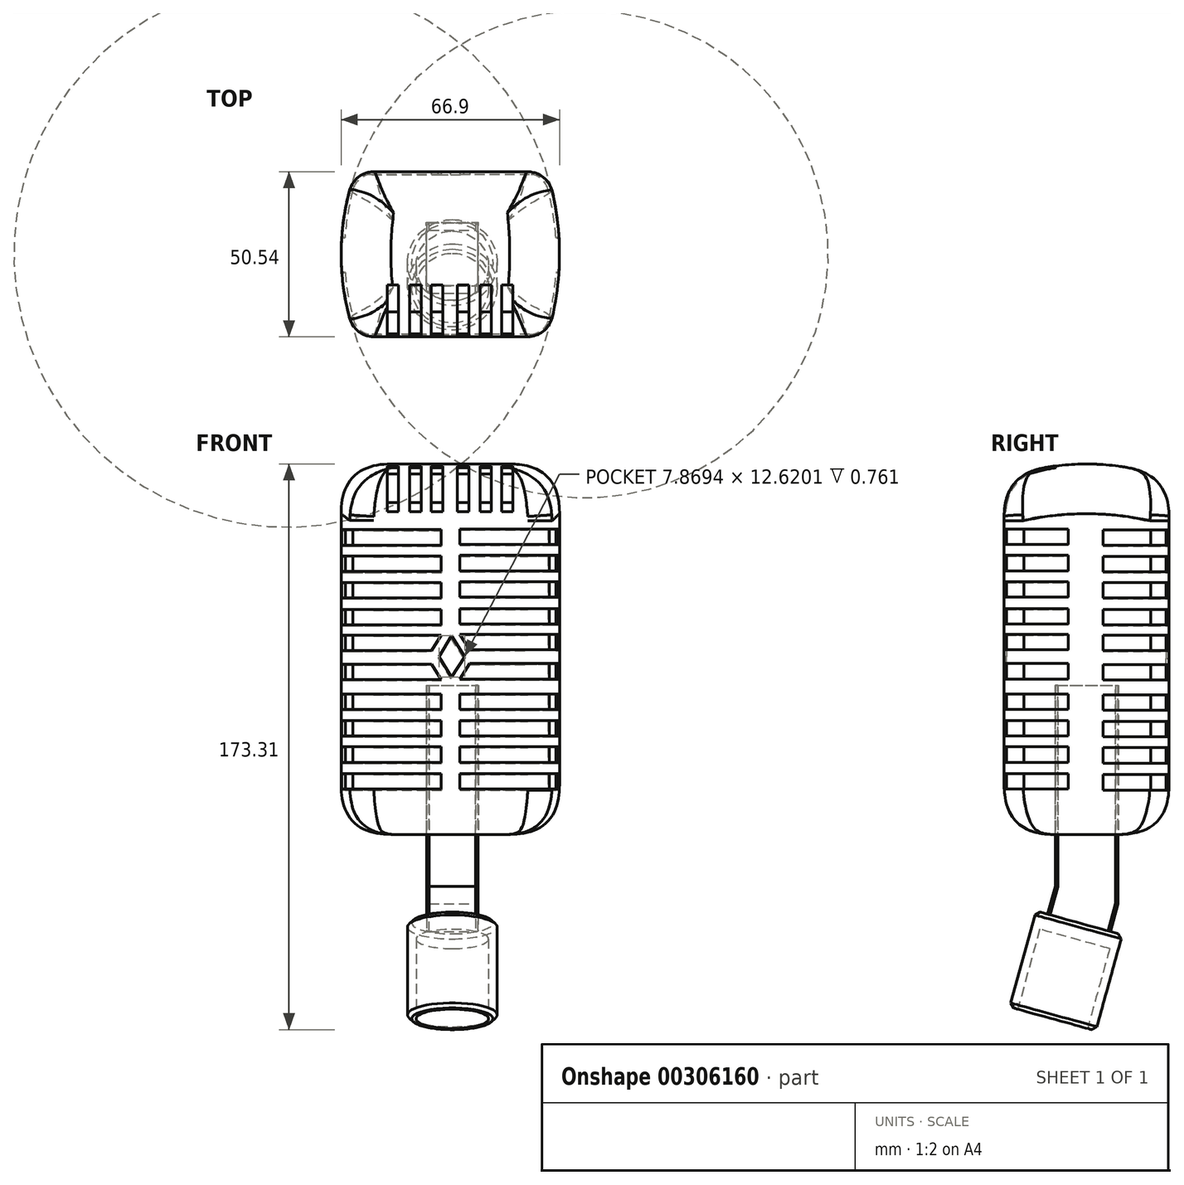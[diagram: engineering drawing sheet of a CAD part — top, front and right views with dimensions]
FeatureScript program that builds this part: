
annotation { "Feature Type Name" : "Feature", "Feature Type Description" : "" }
export const myFeature = defineFeature(function(context is Context, id is Id, definition is map)
    precondition{}
    {
        {
            var Q0;
            Q0=qCreatedBy(makeId("Top.planeOp"),FACE);
            var sketch = newSketch(context, id + "F0", { "sketchPlane" : qUnion([Q0])});
            skLineSegment(sketch, "E0.bottom", {"start": v(-44.56, 25.27) * mm, "end": v(14.03, 25.27) * mm});
            skLineSegment(sketch, "E0.top", {"start": v(-44.56, -25.27) * mm, "end": v(14.03, -25.27) * mm});
            skLineSegment(sketch, "E0.left", {"start": v(-44.56, 25.27) * mm, "end": v(-44.56, -25.27) * mm});
            skLineSegment(sketch, "E0.right", {"start": v(14.03, 25.27) * mm, "end": v(14.03, -25.27) * mm});
            skArc(sketch, "E1", {"start": v(-44.56, 25.27) * mm, "mid": v(-48.96, 0) * mm, "end": v(-44.56, -25.27) * mm});
            skArc(sketch, "E2", {"start": v(14.03, -25.27) * mm, "mid": v(17.94, 0) * mm, "end": v(14.03, 25.27) * mm});
            skSolve(sketch);
        }
        {
            var Q0;
            Q0 = qSketchRegion(id + "F0", true);
            extrude(context, id + "F1", {"entities" : qUnion([Q0]), "depth" : 61.72 * mm, "hasSecondDirection" : true, "secondDirectionOppositeDirection" : true, "secondDirectionDepth" : 52.58 * mm});
        }
        {
            var Q0;
            Q0=qCreatedBy(makeId("Right.planeOp"),FACE);
            cPlane(context, id + "F2", {"entities" : qUnion([Q0]), "cplaneType" : CPlaneType.OFFSET, "offset" : 66.55 * mm, "width" : 152.4 * mm, "height" : 152.4 * mm});
        }
        {
            var Q0;
            Q0=qCreatedBy(id+"F2.planeOp",FACE);
            var sketch = newSketch(context, id + "F3", { "sketchPlane" : qUnion([Q0])});
            skArc(sketch, "E3", {"start": v(-32.43, -60.12) * mm, "mid": v(-0.42, -66.6) * mm, "end": v(31.59, -60.12) * mm});
            skArc(sketch, "E4", {"start": v(31.64, 53.76) * mm, "mid": v(-0.1, 60.92) * mm, "end": v(-31.84, 53.76) * mm});
            skLineSegment(sketch, "E5", {"start": v(-31.84, 53.76) * mm, "end": v(-36.54, 47.04) * mm});
            skLineSegment(sketch, "E6", {"start": v(-36.54, 47.04) * mm, "end": v(-36.54, -49.58) * mm});
            skLineSegment(sketch, "E7", {"start": v(-36.54, -49.58) * mm, "end": v(-32.43, -60.12) * mm});
            skLineSegment(sketch, "E8", {"start": v(31.59, -60.12) * mm, "end": v(40.36, -46.04) * mm});
            skLineSegment(sketch, "E9", {"start": v(40.36, -46.04) * mm, "end": v(40.36, 46.53) * mm});
            skLineSegment(sketch, "E10", {"start": v(40.36, 46.53) * mm, "end": v(31.64, 53.76) * mm});
            skLineSegment(sketch, "E11.bottom", {"start": v(-51.4, 74.25) * mm, "end": v(55.8, 74.25) * mm});
            skLineSegment(sketch, "E11.top", {"start": v(-51.4, -75.1) * mm, "end": v(55.8, -75.1) * mm});
            skLineSegment(sketch, "E11.left", {"start": v(-51.4, 74.25) * mm, "end": v(-51.4, -75.1) * mm});
            skLineSegment(sketch, "E11.right", {"start": v(55.8, 74.25) * mm, "end": v(55.8, -75.1) * mm});
            skSolve(sketch);
        }
        {
            var Q0;
            Q0=makeQuery(id+"F3.imprint","IMPRINT",FACE,{"disambiguationData":[TD([[makeQuery(id+"F3.imprint","IMPRINT",EDGE,{"derivedFrom":sQuery(id+"F3.wireOp",EDGE,"E3")}),-1.0]])]});
            extrude(context, id + "F4", {"entities" : qUnion([Q0]), "operationType" : NewBodyOperationType.REMOVE, "oppositeDirection" : true, "depth" : 198.37 * mm});
        }
        {
            var Q0;
            Q0=makeQuery(id+"F1.opExtrude","SWEPT_EDGE",EDGE,{"disambiguationData":[OSD([sQuery(id+"F0.wireOp",EDGE,"E0.top"),sQuery(id+"F0.wireOp",EDGE,"E0.right"),sQuery(id+"F0.wireOp",EDGE,"E2")])]});
            var Q1;
            Q1=makeQuery(id+"F1.opExtrude","SWEPT_EDGE",EDGE,{"disambiguationData":[OSD([sQuery(id+"F0.wireOp",EDGE,"E0.bottom"),sQuery(id+"F0.wireOp",EDGE,"E0.right"),sQuery(id+"F0.wireOp",EDGE,"E2")])]});
            var Q2;
            Q2=makeQuery(id+"F1.opExtrude","SWEPT_EDGE",EDGE,{"disambiguationData":[OSD([sQuery(id+"F0.wireOp",EDGE,"E0.top"),sQuery(id+"F0.wireOp",EDGE,"E0.left"),sQuery(id+"F0.wireOp",EDGE,"E1")])]});
            var Q3;
            Q3=makeQuery(id+"F1.opExtrude","SWEPT_EDGE",EDGE,{"disambiguationData":[OSD([sQuery(id+"F0.wireOp",EDGE,"E0.bottom"),sQuery(id+"F0.wireOp",EDGE,"E0.left"),sQuery(id+"F0.wireOp",EDGE,"E1")])]});
            fillet(context, id + "F5", {"entities" : qUnion([Q0, Q1, Q2, Q3]), "radius" : 7.62 * mm, "tangentPropagation" : true, "allowEdgeOverflow" : false});
        }
        {
            var Q0;
            Q0=makeQuery(id+"F4.boolean.opBoolean","COPY",FACE,{"derivedFrom":makeQuery(id+"F4.opExtrude","SWEPT_FACE",FACE,{"disambiguationData":[OSD([sQuery(id+"F3.wireOp",EDGE,"E4")])]})});
            var Q1;
            Q1=makeQuery(id+"F4.boolean.opBoolean","COPY",FACE,{"derivedFrom":makeQuery(id+"F4.opExtrude","SWEPT_FACE",FACE,{"disambiguationData":[OSD([sQuery(id+"F3.wireOp",EDGE,"E3")])]})});
            var Q2;
            Q2=makeQuery(id+"F1.opExtrude","CAP_FACE",FACE,{"disambiguationData":[OSD([sQuery(id+"F0.wireOp",EDGE,"E0.bottom"),sQuery(id+"F0.wireOp",EDGE,"E0.top"),sQuery(id+"F0.wireOp",EDGE,"E1"),sQuery(id+"F0.wireOp",EDGE,"E2")])],"isStart":true});
            fillet(context, id + "F6", {"entities" : qUnion([Q0, Q1, Q2]), "radius" : 15.24 * mm, "tangentPropagation" : true, "rho" : 0.5, "crossSection" : FilletCrossSection.CONIC, "allowEdgeOverflow" : false});
        }
        {
            var Q0;
            Q0=qCreatedBy(makeId("Front.planeOp"),FACE);
            cPlane(context, id + "F7", {"entities" : qUnion([Q0]), "cplaneType" : CPlaneType.OFFSET, "offset" : 55.63 * mm, "width" : 152.4 * mm, "height" : 152.4 * mm});
        }
        {
            var Q0;
            Q0=qCreatedBy(id+"F7.planeOp",FACE);
            var sketch = newSketch(context, id + "F8", { "sketchPlane" : qUnion([Q0])});
            skLineSegment(sketch, "E12.bottom", {"start": v(-13.3, 61.66) * mm, "end": v(-9.84, 61.66) * mm});
            skLineSegment(sketch, "E12.top", {"start": v(-13.3, 46.27) * mm, "end": v(-9.84, 46.27) * mm});
            skLineSegment(sketch, "E12.left", {"start": v(-13.3, 61.66) * mm, "end": v(-13.3, 46.27) * mm});
            skLineSegment(sketch, "E12.right", {"start": v(-9.84, 61.66) * mm, "end": v(-9.84, 46.27) * mm});
            skLineSegment(sketch, "E13.bottom", {"start": v(-6.4, 61.66) * mm, "end": v(-2.94, 61.66) * mm});
            skLineSegment(sketch, "E13.top", {"start": v(-6.4, 46.27) * mm, "end": v(-2.94, 46.27) * mm});
            skLineSegment(sketch, "E13.left", {"start": v(-6.4, 61.66) * mm, "end": v(-6.4, 46.27) * mm});
            skLineSegment(sketch, "E13.right", {"start": v(-2.94, 61.66) * mm, "end": v(-2.94, 46.27) * mm});
            skLineSegment(sketch, "E14.bottom", {"start": v(0.21, 61.66) * mm, "end": v(3.67, 61.66) * mm});
            skLineSegment(sketch, "E14.top", {"start": v(0.21, 46.27) * mm, "end": v(3.67, 46.27) * mm});
            skLineSegment(sketch, "E14.left", {"start": v(0.21, 61.66) * mm, "end": v(0.21, 46.27) * mm});
            skLineSegment(sketch, "E14.right", {"start": v(3.67, 61.66) * mm, "end": v(3.67, 46.27) * mm});
            skLineSegment(sketch, "E15.bottom", {"start": v(-34.83, 61.66) * mm, "end": v(-31.37, 61.66) * mm});
            skLineSegment(sketch, "E15.top", {"start": v(-34.83, 46.27) * mm, "end": v(-31.37, 46.27) * mm});
            skLineSegment(sketch, "E15.left", {"start": v(-34.83, 61.66) * mm, "end": v(-34.83, 46.27) * mm});
            skLineSegment(sketch, "E15.right", {"start": v(-31.37, 61.66) * mm, "end": v(-31.37, 46.27) * mm});
            skLineSegment(sketch, "E16.left", {"start": v(-27.93, 61.66) * mm, "end": v(-27.93, 46.27) * mm});
            skLineSegment(sketch, "E16.right", {"start": v(-24.47, 61.66) * mm, "end": v(-24.47, 46.27) * mm});
            skLineSegment(sketch, "E17.left", {"start": v(-21.32, 61.66) * mm, "end": v(-21.32, 46.27) * mm});
            skLineSegment(sketch, "E17.right", {"start": v(-17.86, 61.66) * mm, "end": v(-17.86, 46.27) * mm});
            skLineSegment(sketch, "E18", {"start": v(-27.93, 61.66) * mm, "end": v(-24.47, 61.66) * mm});
            skLineSegment(sketch, "E19", {"start": v(-21.32, 61.66) * mm, "end": v(-17.86, 61.66) * mm});
            skLineSegment(sketch, "E20", {"start": v(-27.93, 46.27) * mm, "end": v(-24.47, 46.27) * mm});
            skLineSegment(sketch, "E21", {"start": v(-21.32, 46.27) * mm, "end": v(-17.86, 46.27) * mm});
            skSolve(sketch);
        }
        {
            var Q0;
            Q0 = qSketchRegion(id + "F8", true);
            extrude(context, id + "F9", {"entities" : qUnion([Q0]), "operationType" : NewBodyOperationType.REMOVE, "oppositeDirection" : true, "depth" : 46.23 * mm});
        }
        {
            var Q0;
            Q0=qCreatedBy(id+"F7.planeOp",FACE);
            var sketch = newSketch(context, id + "F10", { "sketchPlane" : qUnion([Q0])});
            skLineSegment(sketch, "E22", {"start": v(-12.54, 41) * mm, "end": v(26.66, 41) * mm});
            skLineSegment(sketch, "E23", {"start": v(26.66, 41) * mm, "end": v(26.66, 36.27) * mm});
            skLineSegment(sketch, "E24", {"start": v(26.66, 36.27) * mm, "end": v(-12.54, 36.27) * mm});
            skLineSegment(sketch, "E25", {"start": v(-12.54, 36.27) * mm, "end": v(-12.54, 41) * mm});
            skLineSegment(sketch, "E26", {"start": v(-12.54, 32.91) * mm, "end": v(26.66, 32.91) * mm});
            skLineSegment(sketch, "E27", {"start": v(26.66, 32.91) * mm, "end": v(26.66, 28.18) * mm});
            skLineSegment(sketch, "E28", {"start": v(26.66, 28.18) * mm, "end": v(-12.54, 28.18) * mm});
            skLineSegment(sketch, "E29", {"start": v(-12.54, 28.18) * mm, "end": v(-12.54, 32.91) * mm});
            skLineSegment(sketch, "E30", {"start": v(-12.54, 24.84) * mm, "end": v(26.66, 24.84) * mm});
            skLineSegment(sketch, "E31", {"start": v(26.66, 24.84) * mm, "end": v(26.66, 20.11) * mm});
            skLineSegment(sketch, "E32", {"start": v(26.66, 20.11) * mm, "end": v(-12.54, 20.11) * mm});
            skLineSegment(sketch, "E33", {"start": v(-12.54, 20.11) * mm, "end": v(-12.54, 24.84) * mm});
            skLineSegment(sketch, "E34", {"start": v(-12.54, 16.61) * mm, "end": v(26.66, 16.61) * mm});
            skLineSegment(sketch, "E35", {"start": v(26.66, 16.61) * mm, "end": v(26.66, 11.88) * mm});
            skLineSegment(sketch, "E36", {"start": v(26.66, 11.88) * mm, "end": v(-12.54, 11.88) * mm});
            skLineSegment(sketch, "E37", {"start": v(-12.54, 11.88) * mm, "end": v(-12.54, 16.61) * mm});
            skLineSegment(sketch, "E38", {"start": v(-12.54, 8.72) * mm, "end": v(26.66, 8.72) * mm});
            skLineSegment(sketch, "E39", {"start": v(26.66, 8.72) * mm, "end": v(26.66, 3.99) * mm});
            skLineSegment(sketch, "E40", {"start": v(26.66, -0.22) * mm, "end": v(26.66, -4.95) * mm});
            skLineSegment(sketch, "E41", {"start": v(26.66, -4.95) * mm, "end": v(-12.54, -4.95) * mm});
            skLineSegment(sketch, "E42", {"start": v(-57.55, 40.79) * mm, "end": v(-18.34, 40.79) * mm});
            skLineSegment(sketch, "E43", {"start": v(-18.34, 40.79) * mm, "end": v(-18.34, 36.06) * mm});
            skLineSegment(sketch, "E44", {"start": v(-18.34, 36.06) * mm, "end": v(-57.55, 36.06) * mm});
            skLineSegment(sketch, "E45", {"start": v(-57.55, 36.06) * mm, "end": v(-57.55, 40.79) * mm});
            skLineSegment(sketch, "E46", {"start": v(-57.55, 32.7) * mm, "end": v(-18.34, 32.7) * mm});
            skLineSegment(sketch, "E47", {"start": v(-18.34, 32.7) * mm, "end": v(-18.34, 27.97) * mm});
            skLineSegment(sketch, "E48", {"start": v(-18.34, 27.97) * mm, "end": v(-57.55, 27.97) * mm});
            skLineSegment(sketch, "E49", {"start": v(-57.55, 27.97) * mm, "end": v(-57.55, 32.7) * mm});
            skLineSegment(sketch, "E50", {"start": v(-57.55, 24.63) * mm, "end": v(-18.34, 24.63) * mm});
            skLineSegment(sketch, "E51", {"start": v(-18.34, 24.63) * mm, "end": v(-18.34, 19.9) * mm});
            skLineSegment(sketch, "E52", {"start": v(-18.34, 19.9) * mm, "end": v(-57.55, 19.9) * mm});
            skLineSegment(sketch, "E53", {"start": v(-57.55, 16.4) * mm, "end": v(-18.34, 16.4) * mm});
            skLineSegment(sketch, "E54", {"start": v(-18.34, 16.4) * mm, "end": v(-18.34, 11.66) * mm});
            skLineSegment(sketch, "E55", {"start": v(-18.34, 11.66) * mm, "end": v(-57.55, 11.66) * mm});
            skLineSegment(sketch, "E56", {"start": v(-57.55, 11.66) * mm, "end": v(-57.55, 16.4) * mm});
            skLineSegment(sketch, "E57", {"start": v(-57.55, 8.5) * mm, "end": v(-18.34, 8.5) * mm});
            skLineSegment(sketch, "E58", {"start": v(-57.55, 3.77) * mm, "end": v(-57.55, 8.5) * mm});
            skLineSegment(sketch, "E59", {"start": v(-18.34, -5.17) * mm, "end": v(-57.55, -5.17) * mm});
            skLineSegment(sketch, "E60", {"start": v(-57.55, -5.17) * mm, "end": v(-57.55, -0.44) * mm});
            skLineSegment(sketch, "E61", {"start": v(-12.54, -9.58) * mm, "end": v(26.66, -9.58) * mm});
            skLineSegment(sketch, "E62", {"start": v(26.66, -9.58) * mm, "end": v(26.66, -14.31) * mm});
            skLineSegment(sketch, "E63", {"start": v(26.66, -14.31) * mm, "end": v(-12.54, -14.31) * mm});
            skLineSegment(sketch, "E64", {"start": v(-12.54, -14.31) * mm, "end": v(-12.54, -9.58) * mm});
            skLineSegment(sketch, "E65", {"start": v(-12.54, -17.67) * mm, "end": v(26.66, -17.67) * mm});
            skLineSegment(sketch, "E66", {"start": v(26.66, -17.67) * mm, "end": v(26.66, -22.4) * mm});
            skLineSegment(sketch, "E67", {"start": v(26.66, -22.4) * mm, "end": v(-12.54, -22.4) * mm});
            skLineSegment(sketch, "E68", {"start": v(-12.54, -22.4) * mm, "end": v(-12.54, -17.67) * mm});
            skLineSegment(sketch, "E69", {"start": v(-12.54, -25.74) * mm, "end": v(26.66, -25.74) * mm});
            skLineSegment(sketch, "E70", {"start": v(26.66, -25.74) * mm, "end": v(26.66, -30.47) * mm});
            skLineSegment(sketch, "E71", {"start": v(26.66, -30.47) * mm, "end": v(-12.54, -30.47) * mm});
            skLineSegment(sketch, "E72", {"start": v(-12.54, -33.98) * mm, "end": v(26.66, -33.98) * mm});
            skLineSegment(sketch, "E73", {"start": v(26.66, -33.98) * mm, "end": v(26.66, -38.7) * mm});
            skLineSegment(sketch, "E74", {"start": v(26.66, -38.7) * mm, "end": v(-12.54, -38.7) * mm});
            skLineSegment(sketch, "E75", {"start": v(-12.54, -38.7) * mm, "end": v(-12.54, -33.98) * mm});
            skLineSegment(sketch, "E76", {"start": v(-57.5, -9.58) * mm, "end": v(-18.3, -9.58) * mm});
            skLineSegment(sketch, "E77", {"start": v(-18.3, -9.58) * mm, "end": v(-18.3, -14.31) * mm});
            skLineSegment(sketch, "E78", {"start": v(-18.3, -14.31) * mm, "end": v(-57.5, -14.31) * mm});
            skLineSegment(sketch, "E79", {"start": v(-57.5, -14.31) * mm, "end": v(-57.5, -9.58) * mm});
            skLineSegment(sketch, "E80", {"start": v(-57.5, -17.67) * mm, "end": v(-18.3, -17.67) * mm});
            skLineSegment(sketch, "E81", {"start": v(-18.3, -17.67) * mm, "end": v(-18.3, -22.4) * mm});
            skLineSegment(sketch, "E82", {"start": v(-18.3, -22.4) * mm, "end": v(-57.5, -22.4) * mm});
            skLineSegment(sketch, "E83", {"start": v(-57.5, -22.4) * mm, "end": v(-57.5, -17.67) * mm});
            skLineSegment(sketch, "E84", {"start": v(-57.5, -25.74) * mm, "end": v(-18.3, -25.74) * mm});
            skLineSegment(sketch, "E85", {"start": v(-18.3, -25.74) * mm, "end": v(-18.3, -30.47) * mm});
            skLineSegment(sketch, "E86", {"start": v(-18.3, -30.47) * mm, "end": v(-57.5, -30.47) * mm});
            skLineSegment(sketch, "E87", {"start": v(-57.5, -33.98) * mm, "end": v(-18.3, -33.98) * mm});
            skLineSegment(sketch, "E88", {"start": v(-18.3, -33.98) * mm, "end": v(-18.3, -38.7) * mm});
            skLineSegment(sketch, "E89", {"start": v(-18.3, -38.7) * mm, "end": v(-57.5, -38.7) * mm});
            skLineSegment(sketch, "E90", {"start": v(-57.5, -38.7) * mm, "end": v(-57.5, -33.98) * mm});
            skLineSegment(sketch, "E91", {"start": v(-57.55, 24.63) * mm, "end": v(-57.55, 19.9) * mm});
            skLineSegment(sketch, "E92", {"start": v(-57.5, -25.74) * mm, "end": v(-57.5, -30.47) * mm});
            skLineSegment(sketch, "E93", {"start": v(-12.54, -30.47) * mm, "end": v(-12.54, -25.74) * mm});
            skLineSegment(sketch, "E94", {"start": v(-12.54, 8.72) * mm, "end": v(-9.59, 3.99) * mm});
            skLineSegment(sketch, "E95", {"start": v(-9.59, 3.99) * mm, "end": v(26.66, 3.99) * mm});
            skLineSegment(sketch, "E96", {"start": v(-12.54, -4.95) * mm, "end": v(-9.59, -0.22) * mm});
            skLineSegment(sketch, "E97", {"start": v(-9.59, -0.22) * mm, "end": v(26.66, -0.22) * mm});
            skLineSegment(sketch, "E98", {"start": v(-18.34, 8.5) * mm, "end": v(-21.28, 3.77) * mm});
            skLineSegment(sketch, "E99", {"start": v(-21.28, 3.77) * mm, "end": v(-57.55, 3.77) * mm});
            skLineSegment(sketch, "E100", {"start": v(-18.34, -5.17) * mm, "end": v(-21.28, -0.44) * mm});
            skLineSegment(sketch, "E101", {"start": v(-21.28, -0.44) * mm, "end": v(-57.55, -0.44) * mm});
            skLineSegment(sketch, "E102", {"start": v(-15.16, 8.31) * mm, "end": v(-18.95, 1.86) * mm});
            skLineSegment(sketch, "E103", {"start": v(-18.95, 1.86) * mm, "end": v(-15.16, -4.3) * mm});
            skLineSegment(sketch, "E104", {"start": v(-15.16, -4.3) * mm, "end": v(-11.08, 1.86) * mm});
            skLineSegment(sketch, "E105", {"start": v(-11.08, 1.86) * mm, "end": v(-15.16, 8.31) * mm});
            skSolve(sketch);
        }
        {
            var Q0;
            Q0=qCreatedBy(makeId("Front.planeOp"),FACE);
            cPlane(context, id + "F11", {"entities" : qUnion([Q0]), "cplaneType" : CPlaneType.OFFSET, "offset" : 56.64 * mm, "oppositeDirection" : true, "width" : 152.4 * mm, "height" : 152.4 * mm});
        }
        {
            var Q0;
            Q0=qCreatedBy(id+"F11.planeOp",FACE);
            var sketch = newSketch(context, id + "F12", { "sketchPlane" : qUnion([Q0])});
            skLineSegment(sketch, "E106", {"start": v(-12.44, 40.73) * mm, "end": v(26.77, 40.73) * mm});
            skLineSegment(sketch, "E107", {"start": v(26.77, 40.73) * mm, "end": v(26.77, 36) * mm});
            skLineSegment(sketch, "E108", {"start": v(26.77, 36) * mm, "end": v(-12.44, 36) * mm});
            skLineSegment(sketch, "E109", {"start": v(-12.44, 36) * mm, "end": v(-12.44, 40.73) * mm});
            skLineSegment(sketch, "E110", {"start": v(-12.44, 32.64) * mm, "end": v(26.77, 32.64) * mm});
            skLineSegment(sketch, "E111", {"start": v(26.77, 32.64) * mm, "end": v(26.77, 27.91) * mm});
            skLineSegment(sketch, "E112", {"start": v(26.77, 27.91) * mm, "end": v(-12.44, 27.91) * mm});
            skLineSegment(sketch, "E113", {"start": v(-12.44, 27.91) * mm, "end": v(-12.44, 32.64) * mm});
            skLineSegment(sketch, "E114", {"start": v(-12.44, 24.58) * mm, "end": v(26.77, 24.58) * mm});
            skLineSegment(sketch, "E115", {"start": v(26.77, 24.58) * mm, "end": v(26.77, 19.84) * mm});
            skLineSegment(sketch, "E116", {"start": v(26.77, 19.84) * mm, "end": v(-12.44, 19.84) * mm});
            skLineSegment(sketch, "E117", {"start": v(-12.44, 19.84) * mm, "end": v(-12.44, 24.58) * mm});
            skLineSegment(sketch, "E118", {"start": v(-12.44, 16.34) * mm, "end": v(26.77, 16.34) * mm});
            skLineSegment(sketch, "E119", {"start": v(26.77, 16.34) * mm, "end": v(26.77, 11.6) * mm});
            skLineSegment(sketch, "E120", {"start": v(26.77, 11.6) * mm, "end": v(-12.44, 11.6) * mm});
            skLineSegment(sketch, "E121", {"start": v(-12.44, 11.6) * mm, "end": v(-12.44, 16.34) * mm});
            skLineSegment(sketch, "E122", {"start": v(-12.44, 8.45) * mm, "end": v(26.77, 8.45) * mm});
            skLineSegment(sketch, "E123", {"start": v(26.77, 8.45) * mm, "end": v(26.77, 3.72) * mm});
            skLineSegment(sketch, "E124", {"start": v(26.77, -0.5) * mm, "end": v(26.77, -5.22) * mm});
            skLineSegment(sketch, "E125", {"start": v(26.77, -5.22) * mm, "end": v(-12.44, -5.22) * mm});
            skLineSegment(sketch, "E126", {"start": v(-57.45, 40.52) * mm, "end": v(-18.24, 40.52) * mm});
            skLineSegment(sketch, "E127", {"start": v(-18.24, 40.52) * mm, "end": v(-18.24, 35.79) * mm});
            skLineSegment(sketch, "E128", {"start": v(-18.24, 35.79) * mm, "end": v(-57.45, 35.79) * mm});
            skLineSegment(sketch, "E129", {"start": v(-57.45, 35.79) * mm, "end": v(-57.45, 40.52) * mm});
            skLineSegment(sketch, "E130", {"start": v(-57.45, 32.43) * mm, "end": v(-18.24, 32.43) * mm});
            skLineSegment(sketch, "E131", {"start": v(-18.24, 32.43) * mm, "end": v(-18.24, 27.7) * mm});
            skLineSegment(sketch, "E132", {"start": v(-18.24, 27.7) * mm, "end": v(-57.45, 27.7) * mm});
            skLineSegment(sketch, "E133", {"start": v(-57.45, 27.7) * mm, "end": v(-57.45, 32.43) * mm});
            skLineSegment(sketch, "E134", {"start": v(-57.45, 24.36) * mm, "end": v(-18.24, 24.36) * mm});
            skLineSegment(sketch, "E135", {"start": v(-18.24, 24.36) * mm, "end": v(-18.24, 19.63) * mm});
            skLineSegment(sketch, "E136", {"start": v(-18.24, 19.63) * mm, "end": v(-57.45, 19.63) * mm});
            skLineSegment(sketch, "E137", {"start": v(-57.45, 16.13) * mm, "end": v(-18.24, 16.13) * mm});
            skLineSegment(sketch, "E138", {"start": v(-18.24, 16.13) * mm, "end": v(-18.24, 11.4) * mm});
            skLineSegment(sketch, "E139", {"start": v(-18.24, 11.4) * mm, "end": v(-57.45, 11.4) * mm});
            skLineSegment(sketch, "E140", {"start": v(-57.45, 11.4) * mm, "end": v(-57.45, 16.13) * mm});
            skLineSegment(sketch, "E141", {"start": v(-57.45, 8.24) * mm, "end": v(-18.24, 8.24) * mm});
            skLineSegment(sketch, "E142", {"start": v(-57.45, 3.5) * mm, "end": v(-57.45, 8.24) * mm});
            skLineSegment(sketch, "E143", {"start": v(-18.24, -5.44) * mm, "end": v(-57.45, -5.44) * mm});
            skLineSegment(sketch, "E144", {"start": v(-57.45, -5.44) * mm, "end": v(-57.45, -0.7) * mm});
            skLineSegment(sketch, "E145", {"start": v(-12.44, -9.85) * mm, "end": v(26.77, -9.85) * mm});
            skLineSegment(sketch, "E146", {"start": v(26.77, -9.85) * mm, "end": v(26.77, -14.58) * mm});
            skLineSegment(sketch, "E147", {"start": v(26.77, -14.58) * mm, "end": v(-12.44, -14.58) * mm});
            skLineSegment(sketch, "E148", {"start": v(-12.44, -14.58) * mm, "end": v(-12.44, -9.85) * mm});
            skLineSegment(sketch, "E149", {"start": v(-12.44, -17.94) * mm, "end": v(26.77, -17.94) * mm});
            skLineSegment(sketch, "E150", {"start": v(26.77, -17.94) * mm, "end": v(26.77, -22.68) * mm});
            skLineSegment(sketch, "E151", {"start": v(26.77, -22.68) * mm, "end": v(-12.44, -22.68) * mm});
            skLineSegment(sketch, "E152", {"start": v(-12.44, -22.68) * mm, "end": v(-12.44, -17.94) * mm});
            skLineSegment(sketch, "E153", {"start": v(-12.44, -26.01) * mm, "end": v(26.77, -26.01) * mm});
            skLineSegment(sketch, "E154", {"start": v(26.77, -26.01) * mm, "end": v(26.77, -30.74) * mm});
            skLineSegment(sketch, "E155", {"start": v(26.77, -30.74) * mm, "end": v(-12.44, -30.74) * mm});
            skLineSegment(sketch, "E156", {"start": v(-12.44, -34.25) * mm, "end": v(26.77, -34.25) * mm});
            skLineSegment(sketch, "E157", {"start": v(26.77, -34.25) * mm, "end": v(26.77, -38.98) * mm});
            skLineSegment(sketch, "E158", {"start": v(26.77, -38.98) * mm, "end": v(-12.44, -38.98) * mm});
            skLineSegment(sketch, "E159", {"start": v(-12.44, -38.98) * mm, "end": v(-12.44, -34.25) * mm});
            skLineSegment(sketch, "E160", {"start": v(-57.4, -9.85) * mm, "end": v(-18.2, -9.85) * mm});
            skLineSegment(sketch, "E161", {"start": v(-18.2, -9.85) * mm, "end": v(-18.2, -14.58) * mm});
            skLineSegment(sketch, "E162", {"start": v(-18.2, -14.58) * mm, "end": v(-57.4, -14.58) * mm});
            skLineSegment(sketch, "E163", {"start": v(-57.4, -14.58) * mm, "end": v(-57.4, -9.85) * mm});
            skLineSegment(sketch, "E164", {"start": v(-57.4, -17.94) * mm, "end": v(-18.2, -17.94) * mm});
            skLineSegment(sketch, "E165", {"start": v(-18.2, -17.94) * mm, "end": v(-18.2, -22.68) * mm});
            skLineSegment(sketch, "E166", {"start": v(-18.2, -22.68) * mm, "end": v(-57.4, -22.68) * mm});
            skLineSegment(sketch, "E167", {"start": v(-57.4, -22.68) * mm, "end": v(-57.4, -17.94) * mm});
            skLineSegment(sketch, "E168", {"start": v(-57.4, -26.01) * mm, "end": v(-18.2, -26.01) * mm});
            skLineSegment(sketch, "E169", {"start": v(-18.2, -26.01) * mm, "end": v(-18.2, -30.74) * mm});
            skLineSegment(sketch, "E170", {"start": v(-18.2, -30.74) * mm, "end": v(-57.4, -30.74) * mm});
            skLineSegment(sketch, "E171", {"start": v(-57.4, -34.25) * mm, "end": v(-18.2, -34.25) * mm});
            skLineSegment(sketch, "E172", {"start": v(-18.2, -34.25) * mm, "end": v(-18.2, -38.98) * mm});
            skLineSegment(sketch, "E173", {"start": v(-18.2, -38.98) * mm, "end": v(-57.4, -38.98) * mm});
            skLineSegment(sketch, "E174", {"start": v(-57.4, -38.98) * mm, "end": v(-57.4, -34.25) * mm});
            skLineSegment(sketch, "E175", {"start": v(-57.45, 24.36) * mm, "end": v(-57.45, 19.63) * mm});
            skLineSegment(sketch, "E176", {"start": v(-57.4, -26.01) * mm, "end": v(-57.4, -30.74) * mm});
            skLineSegment(sketch, "E177", {"start": v(-12.44, -30.74) * mm, "end": v(-12.44, -26.01) * mm});
            skLineSegment(sketch, "E178", {"start": v(-12.44, 8.45) * mm, "end": v(-9.49, 3.72) * mm});
            skLineSegment(sketch, "E179", {"start": v(-9.49, 3.72) * mm, "end": v(26.77, 3.72) * mm});
            skLineSegment(sketch, "E180", {"start": v(-12.44, -5.22) * mm, "end": v(-9.49, -0.5) * mm});
            skLineSegment(sketch, "E181", {"start": v(-9.49, -0.5) * mm, "end": v(26.77, -0.5) * mm});
            skLineSegment(sketch, "E182", {"start": v(-18.24, 8.24) * mm, "end": v(-21.18, 3.5) * mm});
            skLineSegment(sketch, "E183", {"start": v(-21.18, 3.5) * mm, "end": v(-57.45, 3.5) * mm});
            skLineSegment(sketch, "E184", {"start": v(-18.24, -5.44) * mm, "end": v(-21.18, -0.7) * mm});
            skLineSegment(sketch, "E185", {"start": v(-21.18, -0.7) * mm, "end": v(-57.45, -0.7) * mm});
            skLineSegment(sketch, "E186", {"start": v(-15.36, 7.77) * mm, "end": v(-19.16, 1.32) * mm});
            skLineSegment(sketch, "E187", {"start": v(-19.16, 1.32) * mm, "end": v(-15.36, -4.85) * mm});
            skLineSegment(sketch, "E188", {"start": v(-15.36, -4.85) * mm, "end": v(-11.29, 1.32) * mm});
            skLineSegment(sketch, "E189", {"start": v(-11.29, 1.32) * mm, "end": v(-15.36, 7.77) * mm});
            skSolve(sketch);
        }
        {
            var Q0;
            Q0 = qSketchRegion(id + "F10", true);
            extrude(context, id + "F13", {"entities" : qUnion([Q0]), "operationType" : NewBodyOperationType.REMOVE, "oppositeDirection" : true, "depth" : 50.04 * mm});
        }
        {
            var Q0;
            Q0 = qSketchRegion(id + "F12", true);
            extrude(context, id + "F14", {"entities" : qUnion([Q0]), "operationType" : NewBodyOperationType.REMOVE, "depth" : 51.56 * mm});
        }
        {
            var Q0;
            Q0=qCreatedBy(makeId("Top.planeOp"),FACE);
            cPlane(context, id + "F15", {"entities" : qUnion([Q0]), "cplaneType" : CPlaneType.OFFSET, "offset" : 86.36 * mm, "oppositeDirection" : true, "width" : 152.4 * mm, "height" : 152.4 * mm});
        }
        {
            var Q0;
            Q0=qCreatedBy(id+"F15.planeOp",FACE);
            var sketch = newSketch(context, id + "F16", { "sketchPlane" : qUnion([Q0])});
            skLineSegment(sketch, "E190.bottom", {"start": v(-22.86, -9.65) * mm, "end": v(-6.9, -9.65) * mm});
            skLineSegment(sketch, "E190.top", {"start": v(-22.86, 9.8) * mm, "end": v(-6.9, 9.8) * mm});
            skLineSegment(sketch, "E190.left", {"start": v(-22.86, -9.65) * mm, "end": v(-22.86, 9.8) * mm});
            skLineSegment(sketch, "E190.right", {"start": v(-6.9, -9.65) * mm, "end": v(-6.9, 9.8) * mm});
            skSolve(sketch);
        }
        {
            var Q0;
            Q0 = qSketchRegion(id + "F16", true);
            extrude(context, id + "F17", {"entities" : qUnion([Q0]), "operationType" : NewBodyOperationType.REMOVE, "depth" : 79 * mm});
        }
        {
            var Q0;
            Q0=qCreatedBy(makeId("Top.planeOp"),FACE);
            var sketch = newSketch(context, id + "F18", { "sketchPlane" : qUnion([Q0])});
            skLineSegment(sketch, "E191", {"start": v(-39.5, 24.4) * mm, "end": v(8.78, 24.4) * mm});
            skLineSegment(sketch, "E192", {"start": v(8.78, -24.5) * mm, "end": v(-39.5, -24.5) * mm});
            skArc(sketch, "E193", {"start": v(8.78, -24.5) * mm, "mid": v(12.8, -23) * mm, "end": v(14.83, -19.22) * mm});
            skArc(sketch, "E194", {"start": v(14.43, 19.66) * mm, "mid": v(12.47, 23.07) * mm, "end": v(8.78, 24.4) * mm});
            skArc(sketch, "E195", {"start": v(14.83, -19.22) * mm, "mid": v(17.06, 0.24) * mm, "end": v(14.43, 19.66) * mm});
            skArc(sketch, "E196", {"start": v(-39.5, 24.4) * mm, "mid": v(-43.28, 23.07) * mm, "end": v(-45.37, 19.66) * mm});
            skArc(sketch, "E197", {"start": v(-45.35, -19.22) * mm, "mid": v(-43.44, -23) * mm, "end": v(-39.5, -24.5) * mm});
            skArc(sketch, "E198", {"start": v(-45.37, 19.66) * mm, "mid": v(-47.95, 0.22) * mm, "end": v(-45.35, -19.22) * mm});
            skSolve(sketch);
        }
        {
            var Q0;
            Q0 = qSketchRegion(id + "F18", true);
            extrude(context, id + "F19", {"entities" : qUnion([Q0]), "operationType" : NewBodyOperationType.ADD, "depth" : 44.7 * mm, "hasSecondDirection" : true, "secondDirectionOppositeDirection" : true, "secondDirectionDepth" : 40.9 * mm});
        }
        {
            var Q0;
            Q0=qCreatedBy(makeId("Right.planeOp"),FACE);
            var sketch = newSketch(context, id + "F20", { "sketchPlane" : qUnion([Q0])});
            skLineSegment(sketch, "E199", {"start": v(-24.8, 42.42) * mm, "end": v(-4.43, 42.42) * mm});
            skLineSegment(sketch, "E200", {"start": v(-4.43, 42.42) * mm, "end": v(0, 60.16) * mm});
            skArc(sketch, "E201", {"start": v(-24.37, 49.16) * mm, "mid": v(-24.85, 45.8) * mm, "end": v(-24.8, 42.42) * mm});
            skArc(sketch, "E202", {"start": v(-17.67, 57.87) * mm, "mid": v(-22.04, 54.3) * mm, "end": v(-24.37, 49.16) * mm});
            skArc(sketch, "E203", {"start": v(0, 60.16) * mm, "mid": v(-8.94, 59.8) * mm, "end": v(-17.67, 57.87) * mm});
            skSolve(sketch);
        }
        {
            var Q0;
            Q0 = qSketchRegion(id + "F20", true);
            extrude(context, id + "F21", {"entities" : qUnion([Q0]), "operationType" : NewBodyOperationType.ADD, "depth" : 5.08 * mm, "hasSecondDirection" : true, "secondDirectionOppositeDirection" : true, "secondDirectionDepth" : 35.3 * mm});
        }
        {
            var Q0;
            Q0=makeQuery(id+"F19.opExtrude","CAP_FACE",FACE,{"disambiguationData":[OSD([sQuery(id+"F18.wireOp",EDGE,"E191"),sQuery(id+"F18.wireOp",EDGE,"E192"),sQuery(id+"F18.wireOp",EDGE,"E193"),sQuery(id+"F18.wireOp",EDGE,"E194"),sQuery(id+"F18.wireOp",EDGE,"E195"),sQuery(id+"F18.wireOp",EDGE,"E196"),sQuery(id+"F18.wireOp",EDGE,"E197"),sQuery(id+"F18.wireOp",EDGE,"E198")])],"isStart":true});
            extrude(context, id + "F22", {"entities" : qUnion([Q0]), "operationType" : NewBodyOperationType.REMOVE, "oppositeDirection" : true, "depth" : 34.04 * mm});
        }
        {
            var Q0;
            Q0=makeQuery(id+"F22.boolean.opBoolean","COPY",FACE,{"derivedFrom":makeQuery(id+"F22.opExtrude","CAP_FACE",FACE,{"disambiguationData":[OSD([sQuery(id+"F18.wireOp",EDGE,"E191"),sQuery(id+"F18.wireOp",EDGE,"E192"),sQuery(id+"F18.wireOp",EDGE,"E193"),sQuery(id+"F18.wireOp",EDGE,"E194"),sQuery(id+"F18.wireOp",EDGE,"E195"),sQuery(id+"F18.wireOp",EDGE,"E196"),sQuery(id+"F18.wireOp",EDGE,"E197"),sQuery(id+"F18.wireOp",EDGE,"E198")])],"isStart":false})});
            var sketch = newSketch(context, id + "F23", { "sketchPlane" : qUnion([Q0])});
            skLineSegment(sketch, "E204.bottom", {"start": v(-22.77, 9.57) * mm, "end": v(-7, 9.57) * mm});
            skLineSegment(sketch, "E204.top", {"start": v(-22.77, -9.68) * mm, "end": v(-7, -9.68) * mm});
            skLineSegment(sketch, "E204.left", {"start": v(-22.77, 9.57) * mm, "end": v(-22.77, -9.68) * mm});
            skLineSegment(sketch, "E204.right", {"start": v(-7, 9.57) * mm, "end": v(-7, -9.68) * mm});
            skSolve(sketch);
        }
        {
            var Q0;
            Q0 = qSketchRegion(id + "F23", true);
            extrude(context, id + "F24", {"entities" : qUnion([Q0]), "depth" : 68.07 * mm});
        }
        {
            var Q0;
            Q0=makeQuery(id+"F24.opExtrude","SWEPT_FACE",FACE,{"disambiguationData":[OSD([sQuery(id+"F23.wireOp",EDGE,"E204.right")])]});
            var sketch = newSketch(context, id + "F25", { "sketchPlane" : qUnion([Q0])});
            skLineSegment(sketch, "E205", {"start": v(-16.09, -66.65) * mm, "end": v(31.76, -79.9) * mm});
            skLineSegment(sketch, "E206", {"start": v(31.76, -79.9) * mm, "end": v(-7.36, -91.93) * mm});
            skLineSegment(sketch, "E207", {"start": v(-7.36, -91.93) * mm, "end": v(-16.09, -66.65) * mm});
            skSolve(sketch);
        }
        {
            var Q0;
            Q0 = qSketchRegion(id + "F25", true);
            extrude(context, id + "F26", {"entities" : qUnion([Q0]), "operationType" : NewBodyOperationType.REMOVE, "oppositeDirection" : true, "depth" : 25.4 * mm});
        }
        {
            var Q0;
            Q0=makeQuery(id+"F26.boolean.opBoolean","COPY",FACE,{"derivedFrom":makeQuery(id+"F26.opExtrude","SWEPT_FACE",FACE,{"disambiguationData":[OSD([sQuery(id+"F25.wireOp",EDGE,"E205")])]})});
            extrude(context, id + "F27", {"entities" : qUnion([Q0]), "operationType" : NewBodyOperationType.ADD, "depth" : 8.9 * mm});
        }
        {
            var Q0;
            Q0=makeQuery(id+"F27.opExtrude","CAP_FACE",FACE,{"disambiguationData":[OSD([sQuery(id+"F25.wireOp",EDGE,"E205")])],"isStart":false});
            var sketch = newSketch(context, id + "F28", { "sketchPlane" : qUnion([Q0])});
            skCircle(sketch, "E208", {"center": v(-14.89, -19.07) * mm, "radius": 13.7 * mm});
            skPoint(sketch, "E208.centerSnap0", {"position": v(-14.89, -9.04) * mm});
            skSolve(sketch);
        }
        {
            var Q0;
            Q0 = qSketchRegion(id + "F28", true);
            extrude(context, id + "F29", {"entities" : qUnion([Q0]), "operationType" : NewBodyOperationType.ADD, "depth" : 30.48 * mm});
        }
        {
            var Q0;
            Q0=makeQuery(id+"F29.opExtrude","CAP_FACE",FACE,{"disambiguationData":[OSD([sQuery(id+"F28.wireOp",EDGE,"E208")])],"isStart":false});
            var sketch = newSketch(context, id + "F30", { "sketchPlane" : qUnion([Q0])});
            skCircle(sketch, "E209", {"center": v(-14.89, -19.07) * mm, "radius": 11.1 * mm});
            skSolve(sketch);
        }
        {
            var Q0;
            Q0=makeQuery(id+"F30.imprint","IMPRINT",FACE,{"disambiguationData":[TD([[makeQuery(id+"F30.imprint","IMPRINT",EDGE,{"derivedFrom":sQuery(id+"F30.wireOp",EDGE,"E209")}),1.0]])]});
            extrude(context, id + "F31", {"entities" : qUnion([Q0]), "operationType" : NewBodyOperationType.REMOVE, "oppositeDirection" : true, "depth" : 25.4 * mm});
        }
        {
            var Q0;
            Q0=makeQuery(id+"F29.opExtrude","CAP_EDGE",EDGE,{"disambiguationData":[OSD([sQuery(id+"F28.wireOp",EDGE,"E208")])],"isStart":true});
            var Q1;
            Q1=makeQuery(id+"F29.opExtrude","CAP_EDGE",EDGE,{"disambiguationData":[OSD([sQuery(id+"F28.wireOp",EDGE,"E208")])],"isStart":false});
            chamfer(context, id + "F32", {"entities" : qUnion([Q0, Q1]), "width" : 1.27 * mm, "tangentPropagation" : true});
        }
        {
            var Q0;
            Q0=makeQuery(id+"F24.opExtrude","SWEPT_EDGE",EDGE,{"disambiguationData":[OSD([sQuery(id+"F23.wireOp",EDGE,"E204.bottom"),sQuery(id+"F23.wireOp",EDGE,"E204.right")])]});
            var Q1;
            Q1=makeQuery(id+"F24.opExtrude","SWEPT_EDGE",EDGE,{"disambiguationData":[OSD([sQuery(id+"F23.wireOp",EDGE,"E204.bottom"),sQuery(id+"F23.wireOp",EDGE,"E204.left")])]});
            var Q2;
            Q2=makeQuery(id+"F27.opExtrude","SWEPT_EDGE",EDGE,{"disambiguationData":[OSD([sQuery(id+"F23.wireOp",EDGE,"E204.bottom"),sQuery(id+"F25.wireOp",EDGE,"E205")])]});
            var Q3;
            Q3=makeQuery(id+"F27.opExtrude","SWEPT_EDGE",EDGE,{"disambiguationData":[OSD([sQuery(id+"F23.wireOp",EDGE,"E204.bottom"),sQuery(id+"F23.wireOp",EDGE,"E204.left"),sQuery(id+"F25.wireOp",EDGE,"E205")])]});
            var Q4;
            Q4=makeQuery(id+"F24.opExtrude","SWEPT_EDGE",EDGE,{"disambiguationData":[OSD([sQuery(id+"F23.wireOp",EDGE,"E204.top"),sQuery(id+"F23.wireOp",EDGE,"E204.right")])]});
            var Q5;
            Q5=makeQuery(id+"F27.opExtrude","SWEPT_EDGE",EDGE,{"disambiguationData":[OSD([sQuery(id+"F23.wireOp",EDGE,"E204.top"),sQuery(id+"F25.wireOp",EDGE,"E205")])]});
            var Q6;
            Q6=makeQuery(id+"F27.opExtrude","SWEPT_EDGE",EDGE,{"disambiguationData":[OSD([sQuery(id+"F23.wireOp",EDGE,"E204.top"),sQuery(id+"F23.wireOp",EDGE,"E204.left"),sQuery(id+"F25.wireOp",EDGE,"E205")])]});
            var Q7;
            Q7=makeQuery(id+"F24.opExtrude","SWEPT_EDGE",EDGE,{"disambiguationData":[OSD([sQuery(id+"F23.wireOp",EDGE,"E204.top"),sQuery(id+"F23.wireOp",EDGE,"E204.left")])]});
            chamfer(context, id + "F33", {"entities" : qUnion([Q0, Q1, Q2, Q3, Q4, Q5, Q6, Q7]), "width" : 0.76 * mm, "tangentPropagation" : true});
        }
    });
